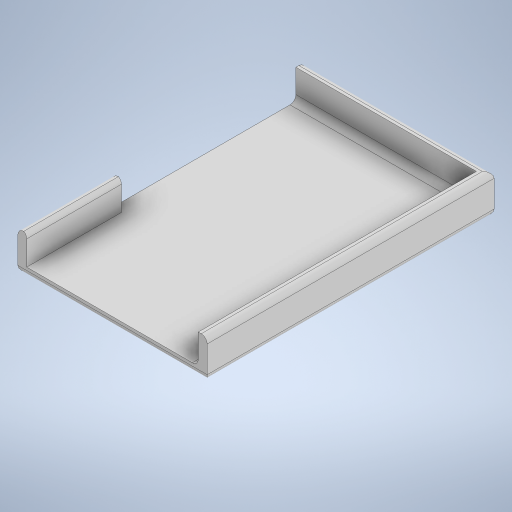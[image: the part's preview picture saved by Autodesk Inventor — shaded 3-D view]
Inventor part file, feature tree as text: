
AUTODESK INVENTOR PART (.ipt)
format: ipt  version: 2023 (Build 270158000, 158)  size: 326,656 bytes
history: native  units: mm
features: extrude x5, sketch x5, chamfer x4, fillet x2, other x1
ambient origin geometry x8: Origin, YZ Plane, XZ Plane, XY Plane, X Axis, Y Axis, Z Axis, Center Point
bodies: Body1 (feature_tree)
feature tree (17):
  other  "Bryła1"
  extrude  "Wyciągnięcie proste1"  Depth=97.0mm
  extrude  "Wyciągnięcie proste2"  Depth=64.0mm
  extrude  "Wyciągnięcie proste3"  Depth=3.0mm TaperAngle=0.0deg
  extrude  "Wyciągnięcie proste4"  Depth=3.0mm
  chamfer  "Faza1"  Distance=3.0mm
  chamfer  "Faza2"  Distance=10.0mm
  chamfer  "Faza3"  Distance=3.0mm
  chamfer  "Faza4"  Distance=62.0mm
  extrude  "Wyciągnięcie proste5"  Depth=10.0mm TaperAngle=0.0deg
  fillet  "Zaokrąglenie1"  Radius=18.0mm
  fillet  "Zaokrąglenie2"  Radius=18.0mm
  sketch  "Szkic1"
  sketch  "Szkic2"
  sketch  "Szkic3"
  sketch  "Szkic4"
  sketch  "Szkic5"
